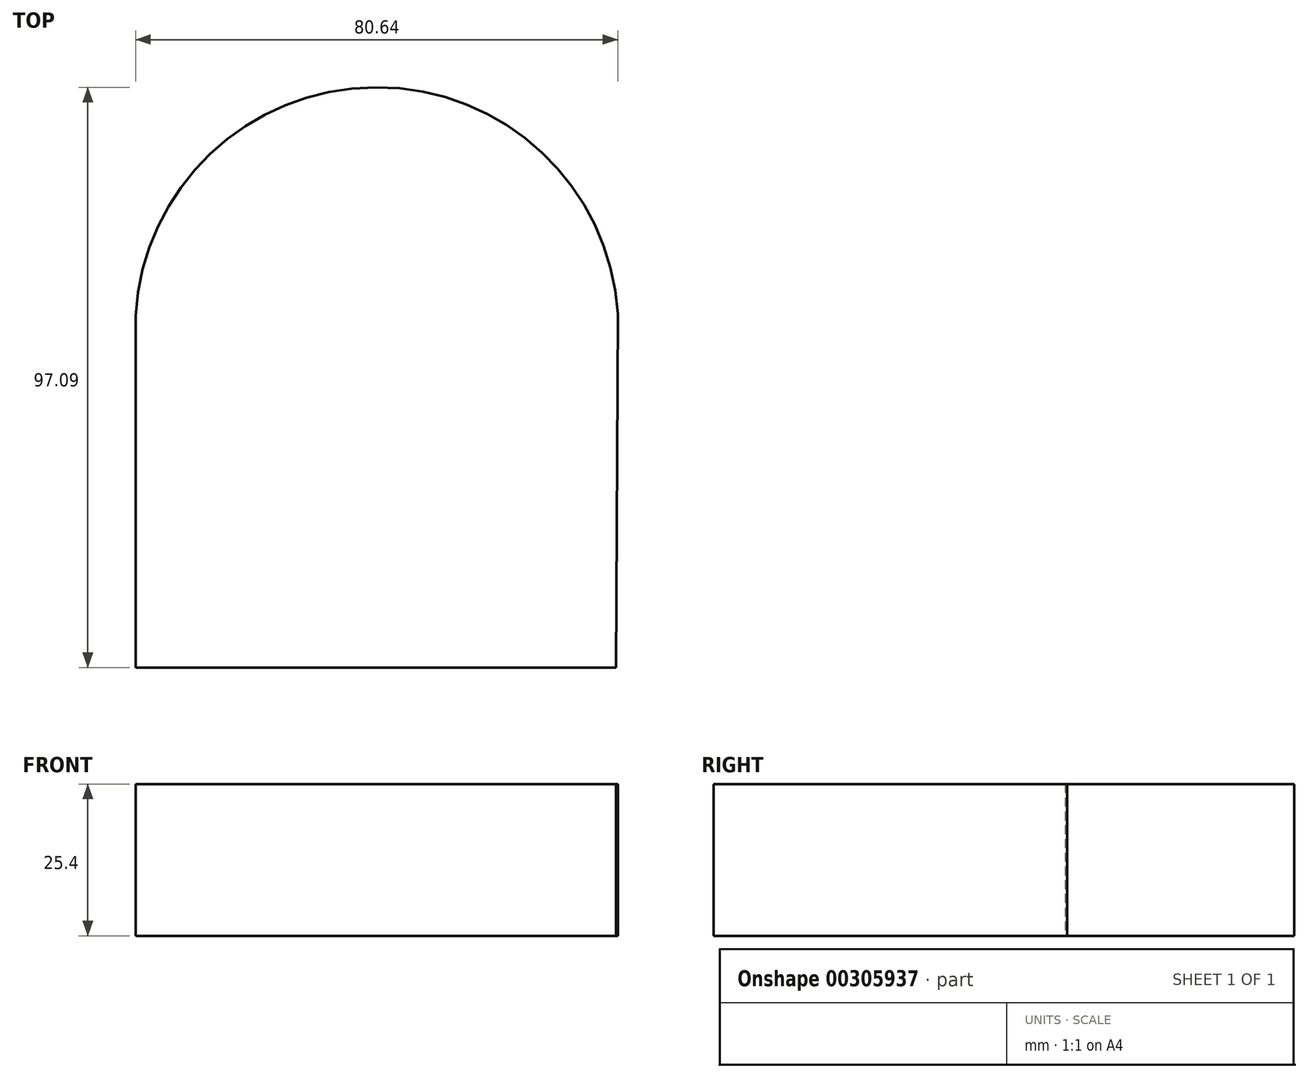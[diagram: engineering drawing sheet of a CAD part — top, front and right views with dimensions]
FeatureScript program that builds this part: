
annotation { "Feature Type Name" : "Feature", "Feature Type Description" : "" }
export const myFeature = defineFeature(function(context is Context, id is Id, definition is map)
    precondition{}
    {
        {
            var Q0;
            Q0=qCreatedBy(makeId("Top.planeOp"),FACE);
            var sketch = newSketch(context, id + "F0", { "sketchPlane" : qUnion([Q0])});
            skArc(sketch, "E0", {"start": v(41.1, 21.8) * mm, "mid": v(0.63, 59.74) * mm, "end": v(-39.54, 21.5) * mm});
            skLineSegment(sketch, "E1", {"start": v(-39.54, 21.5) * mm, "end": v(-39.54, -37.35) * mm});
            skLineSegment(sketch, "E2", {"start": v(-39.54, -37.35) * mm, "end": v(40.79, -37.35) * mm});
            skLineSegment(sketch, "E3", {"start": v(40.79, -37.35) * mm, "end": v(41.1, 21.8) * mm});
            skSolve(sketch);
        }
        {
            var Q0;
            Q0 = qSketchRegion(id + "F0", true);
            extrude(context, id + "F1", {"entities" : qUnion([Q0]), "depth" : 25.4 * mm});
        }
    });
